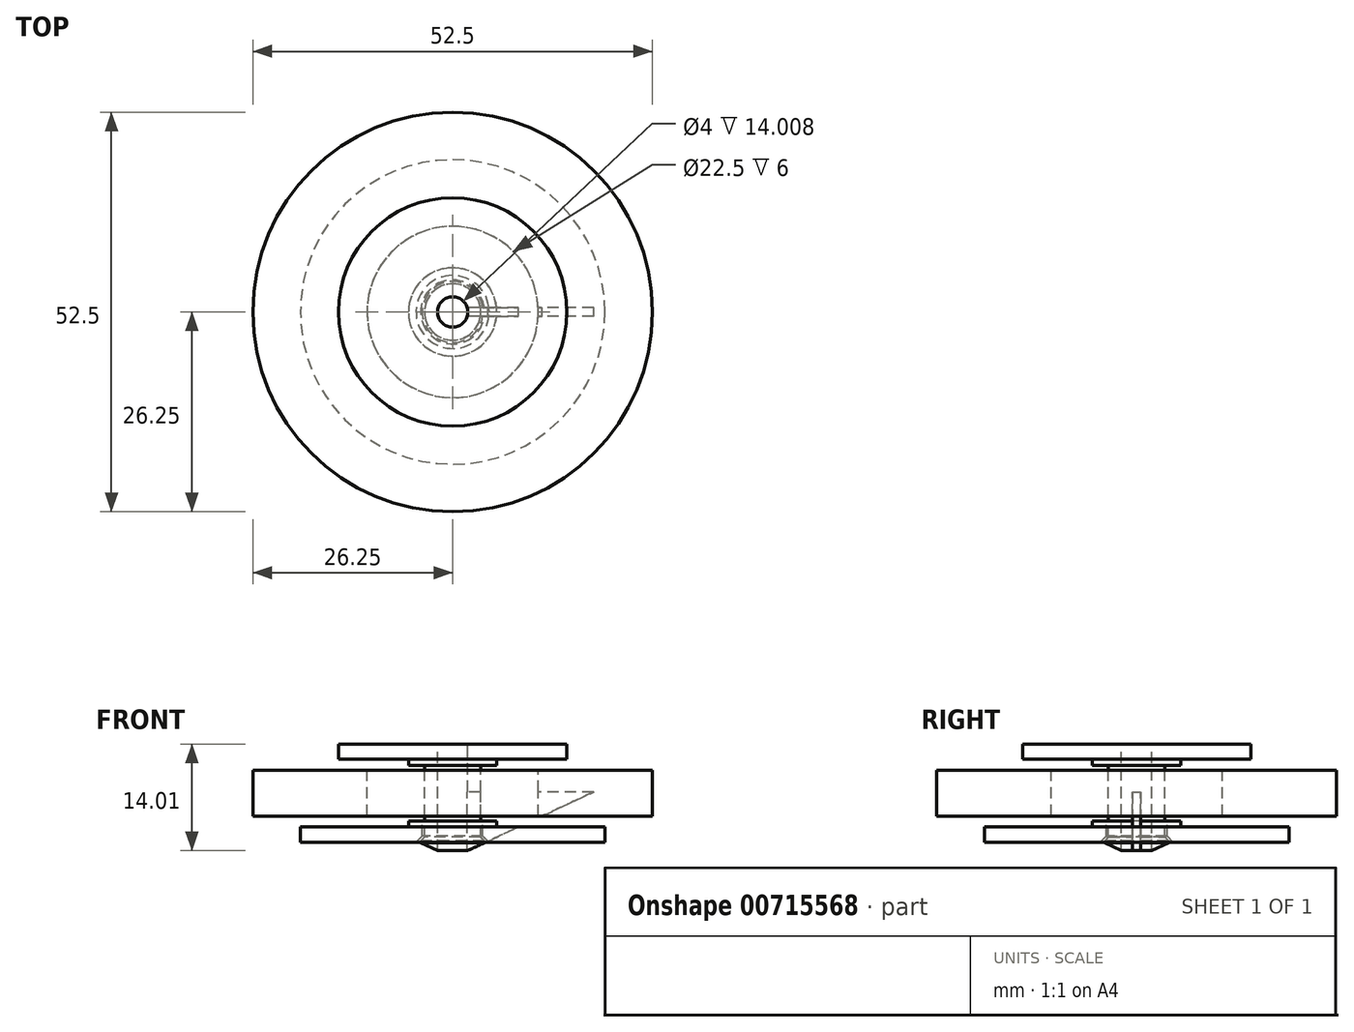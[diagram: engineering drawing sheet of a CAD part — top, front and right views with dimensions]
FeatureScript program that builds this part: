
annotation { "Feature Type Name" : "Feature", "Feature Type Description" : "" }
export const myFeature = defineFeature(function(context is Context, id is Id, definition is map)
    precondition{}
    {
        {
            var Q0;
            Q0=qCreatedBy(makeId("Front.planeOp"),FACE);
            var sketch = newSketch(context, id + "F0", { "sketchPlane" : qUnion([Q0])});
            skLineSegment(sketch, "E0", {"start": v(0, 86.94) * mm, "end": v(0, -87.04) * mm, "construction": true});
            skLineSegment(sketch, "E1", {"start": v(-2, 0) * mm, "end": v(-15, 0) * mm});
            skLineSegment(sketch, "E2", {"start": v(-15, 0) * mm, "end": v(-15, -2) * mm});
            skLineSegment(sketch, "E3", {"start": v(-3.7, -2.8) * mm, "end": v(-3.7, -12.22) * mm});
            skLineSegment(sketch, "E4", {"start": v(-3.7, -12.22) * mm, "end": v(-4.2, -12.72) * mm});
            skLineSegment(sketch, "E5", {"start": v(-4.2, -12.9) * mm, "end": v(-2, -12.9) * mm, "construction": true});
            skLineSegment(sketch, "E6", {"start": v(-2, 0) * mm, "end": v(-2, -12.9) * mm});
            skLineSegment(sketch, "E7", {"start": v(-4, -12.1) * mm, "end": v(-4.8, -12.9) * mm});
            skLineSegment(sketch, "E8", {"start": v(-4.8, -12.9) * mm, "end": v(-20, -12.9) * mm});
            skLineSegment(sketch, "E9", {"start": v(-4.8, -10.1) * mm, "end": v(-4.8, -10.1) * mm});
            skLineSegment(sketch, "E10", {"start": v(-4.8, -10.1) * mm, "end": v(-4, -10.1) * mm});
            skLineSegment(sketch, "E11", {"start": v(-4, -10.1) * mm, "end": v(-4, -12.1) * mm});
            skLineSegment(sketch, "E12", {"start": v(-20, -12.9) * mm, "end": v(-20, -10.9) * mm});
            skLineSegment(sketch, "E13", {"start": v(-20, -10.9) * mm, "end": v(-5.8, -10.9) * mm});
            skLineSegment(sketch, "E14", {"start": v(-5.8, -10.9) * mm, "end": v(-5.8, -10.1) * mm});
            skLineSegment(sketch, "E15", {"start": v(-5.8, -10.1) * mm, "end": v(-4.8, -10.1) * mm});
            skLineSegment(sketch, "E16", {"start": v(-3.7, -2.8) * mm, "end": v(-5.8, -2.8) * mm});
            skLineSegment(sketch, "E17", {"start": v(-5.8, -2.8) * mm, "end": v(-5.8, -2) * mm});
            skLineSegment(sketch, "E18", {"start": v(-5.8, -2) * mm, "end": v(-15, -2) * mm});
            skLineSegment(sketch, "E19.bottom", {"start": v(-26.25, -9.45) * mm, "end": v(-11.25, -9.45) * mm});
            skLineSegment(sketch, "E19.top", {"start": v(-26.25, -3.45) * mm, "end": v(-11.25, -3.45) * mm});
            skLineSegment(sketch, "E19.left", {"start": v(-26.25, -9.45) * mm, "end": v(-26.25, -3.45) * mm});
            skLineSegment(sketch, "E19.right", {"start": v(-11.25, -9.45) * mm, "end": v(-11.25, -3.45) * mm});
            skPoint(sketch, "E19.middle", {"position": v(-18.75, -6.45) * mm});
            skLineSegment(sketch, "E20", {"start": v(-4.2, -12.98) * mm, "end": v(-2, -14) * mm});
            skLineSegment(sketch, "E21", {"start": v(-2, -14) * mm, "end": v(-2, -12.9) * mm});
            skLineSegment(sketch, "E22", {"start": v(-4.2, -12.98) * mm, "end": v(-4.2, -12.72) * mm});
            skPoint(sketch, "E23.orphan", {"position": v(-4.38, -12.9) * mm});
            skLineSegment(sketch, "E24", {"start": v(-18.75, -6.45) * mm, "end": v(-18.75, -12.9) * mm, "construction": true});
            skLineSegment(sketch, "E25", {"start": v(-18.75, -6.45) * mm, "end": v(-18.75, 0) * mm, "construction": true});
            skSolve(sketch);
        }
        {
            var Q0;
            Q0=qSketchRegion(id+"F0",true);
            var Q1;
            Q1=sQuery(id+"F0.wireOp",EDGE,"E0");
            revolve(context, id + "F1", {"surfaceOperationType" : NewSurfaceOperationType.NEW, "entities" : qUnion([Q0]), "axis" : qUnion([Q1]), "revolveType" : RevolveType.FULL});
        }
        {
            var Q0;
            Q0=qCreatedBy(makeId("Right.planeOp"),FACE);
            var sketch = newSketch(context, id + "F2", { "sketchPlane" : qUnion([Q0])});
            skLineSegment(sketch, "E26.0", {"start": v(-5.8, -2.8) * mm, "end": v(5.8, -2.8) * mm, "construction": true});
            skLineSegment(sketch, "E27.bottom", {"start": v(-0.55, -6.3) * mm, "end": v(0.55, -6.3) * mm});
            skLineSegment(sketch, "E27.top", {"start": v(-0.55, -14) * mm, "end": v(0.55, -14) * mm});
            skLineSegment(sketch, "E27.left", {"start": v(-0.55, -6.3) * mm, "end": v(-0.55, -14) * mm});
            skLineSegment(sketch, "E27.right", {"start": v(0.55, -6.3) * mm, "end": v(0.55, -14) * mm});
            skPoint(sketch, "E27.middle", {"position": v(0, -10.15) * mm});
            skLineSegment(sketch, "E28.0", {"start": v(-2, -14) * mm, "end": v(2, -14) * mm, "construction": true});
            skSolve(sketch);
        }
        {
            var Q0;
            Q0=makeQuery(id+"F2.imprint","IMPRINT",FACE,{"disambiguationData":[TD([[makeQuery(id+"F2.imprint","IMPRINT",EDGE,{"derivedFrom":sQuery(id+"F2.wireOp",EDGE,"E27.bottom")}),-1.0]])]});
            var Q1;
            Q1=makeQuery(id+"F1.opRevolve","SWEPT_FACE",FACE,{"disambiguationData":[OSD([sQuery(id+"F0.wireOp",EDGE,"E20")])]});
            extrude(context, id + "F3", {"entities" : qUnion([Q0]), "operationType" : NewBodyOperationType.REMOVE, "endBound" : BoundingType.UP_TO_SURFACE, "depth" : 25 * mm, "endBoundEntityFace" : qUnion([Q1]), "offsetDistance" : 25 * mm});
        }
    });
